# Revit family: 1 SOUND_Panorama_Freestanding
name_source: partatom
category: Communication Devices
units: mm (PartAtom-declared; Revit-internal decimal feet)

## family parameters
Always vertical = No
Cut with Voids When Loaded = No
Maintain Annotation Orientation = No
Part Type = Normal
Room Calculation Point = No
Round Connector Dimension = Use Diameter
Shared = No
Work Plane-Based = Yes

## types (1)
- MS34
    Bandwidth = 95 Hz - 18 kHz (-6 dB)
    Category = Speaker
    Connectors = (2) NL4 plus a switch which changes M+S mode to ono (line source) mode
    Construction = Finland birch ply (phenolic glue), polyurea, clear matte salt and UV resistant coating, 316 stainless steel hardware, 3D spacer mesh fabric
    Default Elevation = 0 mm
    Dimensions (HxWxD) = 346.00mm x 144mm x 197mm
    Height Overall = 144 mm
    Impedance = 16Ω + 16Ω
    Manufacturer = 1 SOUND
    Model = MS34
    Power = 200+200 watts (continuous), 100+100 watts (AES)
    Rigging = (2) M6 points
    URL = https://www.1-sound.com
    Weight = 4.30 kg

## geometry (parser evidence)
native form markers: Sweep x9
no freeform markers — native parametric forms only
